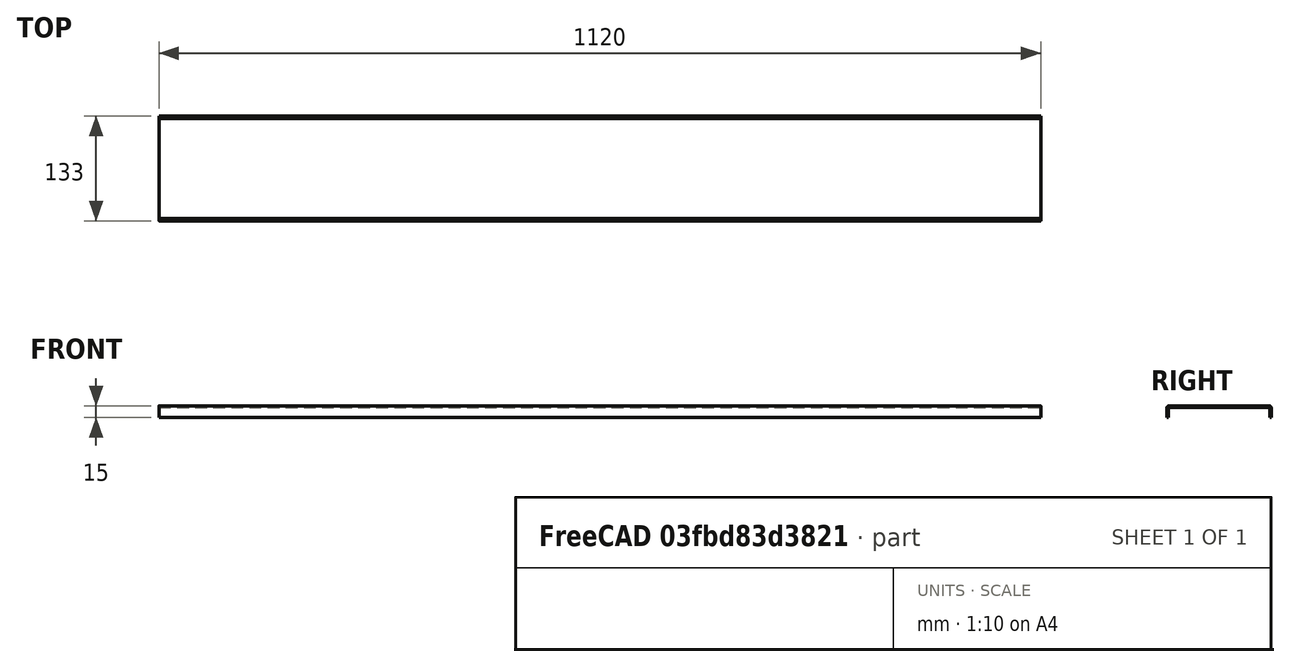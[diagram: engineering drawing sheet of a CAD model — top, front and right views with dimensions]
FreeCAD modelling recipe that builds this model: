
FCSTD DOCUMENT  (FreeCAD 0.17R13528 (Git))
Label: SupportClavierSuperieur
License: All rights reserved
LicenseURL: http://en.wikipedia.org/wiki/All_rights_reserved
objects: Drawing::FeatureViewPart×3, Drawing::FeatureViewPython×3, Part::FeaturePython×2, Part::Box×1, PartDesign::FeatureBase×1, PartDesign::Body×1, Drawing::FeaturePage×1
note: 5 computed .brp shape members not serialized (recipe doc carries the construction recipe); baked Part::Feature solids carry a one-line shape summary decoded from their .brp

FEATURE [Part::Box] Box  label="Cube"
  AttacherType = Attacher::AttachEngine3D
  Height = 2
  Length = 1120
  Width = 127
FEATURE [Part::FeaturePython] Bend  # WARN: FeaturePython — macro-defined, semantics opaque (R4)
  angle = 90
  baseObject = -> Box [Face3]
  gap1 = 0
  gap2 = 0
  invert = true
  length = 12
  radius = 1
  reliefd = 1
  reliefw = 0.5
FEATURE [Part::FeaturePython] Bend001  # WARN: FeaturePython — macro-defined, semantics opaque (R4)
  angle = 90
  baseObject = -> Bend [Face14]
  gap1 = 0
  gap2 = 0
  invert = true
  length = 12
  radius = 1
  reliefd = 1
  reliefw = 0.5
FEATURE [PartDesign::FeatureBase] BaseFeature
  BaseFeature = -> Bend001
FEATURE [PartDesign::Body] Body
  BaseFeature = -> Bend001
  Group = -> [BaseFeature]
  Origin = -> Origin
  Tip = -> BaseFeature
FEATURE [Drawing::FeatureViewPart] Ortho  label="Ortho_0_0"
  Direction = (0,0,1)
  HiddenWidth = 0.15
  LineWidth = 0.35
  Rotation = 0
  Scale = 0.2
  ShowHiddenLines = false
  ShowSmoothLines = false
  Source = -> Body
  Tolerance = 0.05
  ViewResult = <g id="Ortho_0_0"\n   transform="rotate(0,26.6667,120.6) translate(26.6667,120.6) scale(0.2,0.2)"\n  >\n<g   fill="none"\n   stroke="rgb(0, 0, 0)"\n   stroke-linecap="butt"\n   stroke-linejoin="miter"\n   stroke-width="1.750000"\n   transform="scale(1,-1)"\n  >\n<path id= "1" d=" M 0 130 L 1120 130 " />\n<path d="M1120,127 L1120,127.336  L1120,127.668  L1120,127.991  L1120,128.302  L1120,128.596  L1120,128.87  L1120,129.121  L1120,129.345  L1120,129.54  L1120,129.703  L1120,129.832  L1120,129.925  L1120,129.981  L1120,130 " /><path id= "3" d=" M 0 127 L 1120 127 " />\n<path d="M0,127 L0,127.336  L0,127.668  L0,127.991  L0,128.302  L0,128.596  L0,128.87  L0,129.121  L0,129.345  L0,129.54  L0,129.703  L0,129.832  L0,129.925  L0,129.981  L0,130 " /><path id= "5" d=" M 1120 0 L 1120 127 " />\n<path id= "6" d=" M 0 0 L 0 127 " />\n<path id= "7" d=" M 0 0 L 1120 0 " />\n<path d="M1120,0 L1120,-0.335893  L1120,-0.667563  L1120,-0.990837  L1120,-1.30165  L1120,-1.5961  L1120,-1.87047  L1120,-2.12132  L1120,-2.34549  L1120,-2.54017  L1120,-2.70291  L1120,-2.83165  L1120,-2.92478  L1120,-2.98114  L1120,-3 " /><path id= "9" d=" M 0 -3 L 1120 -3 " />\n<path d="M0,0 L0,-0.335893  L0,-0.667563  L0,-0.990837  L0,-1.30165  L0,-1.5961  L0,-1.87047  L0,-2.12132  L0,-2.34549  L0,-2.54017  L0,-2.70291  L0,-2.83165  L0,-2.92478  L0,-2.98114  L0,-3 " /></g>\n</g>
  Visible = false
  X = 26.6667
  Y = 120.6
FEATURE [Drawing::FeatureViewPart] Ortho001  label="Ortho_1_0"
  Direction = (-1,0,0)
  HiddenWidth = 0.15
  LineWidth = 0.35
  Rotation = 180
  Scale = 0.2
  ShowHiddenLines = false
  ShowSmoothLines = false
  Source = -> Body
  Tolerance = 0.05
  ViewResult = <g id="Ortho_1_0"\n   transform="rotate(180,269.933,120.6) translate(269.933,120.6) scale(0.2,0.2)"\n  >\n<g   fill="none"\n   stroke="rgb(0, 0, 0)"\n   stroke-linecap="butt"\n   stroke-linejoin="miter"\n   stroke-width="1.750000"\n   transform="scale(1,-1)"\n  >\n<path id= "1" d=" M 13 -128 L 13 -130 " />\n<path id= "2" d=" M 1 -128 L 13 -128 " />\n<path id= "3" d=" M 1 -130 L 13 -130 " />\n<path id= "4" d=" M 1 -128 L 1 -130 " />\n<path d="M0 -127 A1 1 0 0 1 1 -128" /><path d="M-2 -127 A3 3 0 0 1 1 -130" /><path id= "7" d=" M 0 -127 L -2 -127 " />\n<path id= "8" d=" M 0 0 L 0 -127 " />\n<path id= "9" d=" M -2 0 L -2 -127 " />\n<path id= "10" d=" M 0 0 L -2 0 " />\n<path d="M0 0 A1 1 0 0 0 1 1" /><path d="M-2 0 A3 3 0 0 0 1 3" /><path id= "13" d=" M 1 1 L 1 3 " />\n<path id= "14" d=" M 1 1 L 13 1 " />\n<path id= "15" d=" M 1 3 L 13 3 " />\n<path id= "16" d=" M 13 1 L 13 3 " />\n</g>\n</g>
  Visible = false
  X = 269.933
  Y = 120.6
FEATURE [Drawing::FeatureViewPart] Ortho002  label="Ortho_0_1"
  Direction = (0,-1,0)
  HiddenWidth = 0.15
  LineWidth = 0.35
  Rotation = 90
  Scale = 0.2
  ShowHiddenLines = false
  ShowSmoothLines = false
  Source = -> Body
  Tolerance = 0.05
  ViewResult = <g id="Ortho_0_1"\n   transform="rotate(90,26.6667,51.2) translate(26.6667,51.2) scale(0.2,0.2)"\n  >\n<g   fill="none"\n   stroke="rgb(0, 0, 0)"\n   stroke-linecap="butt"\n   stroke-linejoin="miter"\n   stroke-width="1.750000"\n   transform="scale(1,-1)"\n  >\n<path id= "1" d=" M -2 0 L -2 1120 " />\n<path d="M-2,1120 Q-1.99057,1120 -1.98114,1120  Q-1.95296,1120 -1.92478,1120  Q-1.87822,1120 -1.83165,1120  Q-1.76728,1120 -1.70291,1120  Q-1.62154,1120 -1.54017,1120  Q-1.44283,1120 -1.34549,1120  Q-1.23341,1120 -1.12132,1120  Q-0.995895,1120 -0.870469,1120  Q-0.733283,1120 -0.596096,1120  Q-0.448874,1120 -0.301651,1120  Q-0.146244,1120 0.00916281,1120  Q0.1708,1120 0.332437,1120  Q0.662922,1120 1,1120 " /><path id= "3" d=" M 1 0 L 1 1120 " />\n<path d="M-2,0 Q-1.99057,0 -1.98114,0  Q-1.95296,0 -1.92478,0  Q-1.87822,0 -1.83165,0  Q-1.76728,0 -1.70291,0  Q-1.62154,0 -1.54017,0  Q-1.44283,0 -1.34549,0  Q-1.23341,0 -1.12132,0  Q-0.995895,0 -0.870469,0  Q-0.733283,0 -0.596096,0  Q-0.448874,0 -0.301651,0  Q-0.146244,0 0.00916281,0  Q0.1708,0 0.332437,0  Q0.662922,0 1,0 " /><path id= "5" d=" M 1 1120 L 13 1120 " />\n<path id= "6" d=" M 13 0 L 13 1120 " />\n<path id= "7" d=" M 1 0 L 13 0 " />\n</g>\n</g>
  Visible = false
  X = 26.6667
  Y = 51.2
FEATURE [Drawing::FeatureViewPython] dim001  # drawing view (typed FeaturePython)
  Rotation = 0
  ViewResult = <g> \n  <line x1="26.666700" y1="55.800000" x2="26.666700" y2="66.000000" style="stroke:rgb(0,0,255);stroke-width:0.30" />\n<line x1="250.666700" y1="55.800000" x2="250.666700" y2="66.000000" style="stroke:rgb(0,0,255);stroke-width:0.30" />\n<line x1="26.666700" y1="65.000000" x2="250.666700" y2="65.000000" style="stroke:rgb(0,0,255);stroke-width:0.30" /> \n  <polygon points="250.666700,65.000000 247.666700,64.000000 246.666700,65.000000 247.666700,66.000000" style="fill:rgb(0,0,255);stroke:rgb(0,0,255);stroke-width:0" /><polygon points="26.666700,65.000000 29.666700,66.000000 30.666700,65.000000 29.666700,64.000000" style="fill:rgb(0,0,255);stroke:rgb(0,0,255);stroke-width:0" /> \n  <text x="138.666700" y="63.000000" font-family="Verdana" font-size="3.6" fill="rgb(0,0,255)" text-anchor="middle" transform="rotate(0.000000 138.666700,63.000000)" >1120</text> </g>
  Visible = false
  X = 0
  Y = 0
  arrowL1 = 3
  arrowL2 = 1
  arrowW = 2
  arrow_scheme = 0
  autoPlaceOffset = 2
  autoPlaceText = true
  click1_x = 125
  click1_y = 65
  click2_x = 125
  click2_y = 65
  comma_decimal_place = false
  dimension_line_overshoot = 1
  gap_datum_points = 2
  halfDimension_linear = false
  lineColor = rgb(0,0,255)
  strokeWidth = 0.3
  textFormat_linear = %(value)3.0f
  textRenderer_color = rgb(0,0,255)
  textRenderer_family = Verdana
  textRenderer_size = 3.6
  unit_custom_scale = 1
  unit_scheme = 0
FEATURE [Drawing::FeatureViewPython] dim002  # drawing view (typed FeaturePython)
  Rotation = 0
  ViewResult = <g> <line x1="24.666700" y1="94.600000" x2="19.000000" y2="94.600000" style="stroke:rgb(0,0,255);stroke-width:0.30" />\n<line x1="24.666700" y1="121.200000" x2="19.000000" y2="121.200000" style="stroke:rgb(0,0,255);stroke-width:0.30" />\n<line x1="20.000000" y1="94.600000" x2="20.000000" y2="121.200000" style="stroke:rgb(0,0,255);stroke-width:0.30" />\n<polygon points="20.000000,94.600000 19.000000,97.600000 20.000000,98.600000 21.000000,97.600000" style="fill:rgb(0,0,255);stroke:rgb(0,0,255);stroke-width:0" />\n<polygon points="20.000000,121.200000 21.000000,118.200000 20.000000,117.200000 19.000000,118.200000" style="fill:rgb(0,0,255);stroke:rgb(0,0,255);stroke-width:0" />\n<text x="18.000000" y="107.900000" font-family="Verdana" font-size="3.6" fill="rgb(0,0,255)" text-anchor="middle" transform="rotate(-90.000000 18.000000,107.900000)" >133</text> </g> 
  Visible = false
  X = 0
  Y = 0
  arrowL1 = 3
  arrowL2 = 1
  arrowW = 2
  arrow_scheme = 0
  autoPlaceOffset = 2
  autoPlaceText = true
  click1_x = 20
  click1_y = 120
  click2_x = 20
  click2_y = 120
  comma_decimal_place = false
  dimension_line_overshoot = 1
  gap_datum_points = 2
  halfDimension_linear = false
  lineColor = rgb(0,0,255)
  strokeWidth = 0.3
  textFormat_linear = %(value)3.0f
  textRenderer_color = rgb(0,0,255)
  textRenderer_family = Verdana
  textRenderer_size = 3.6
  unit_custom_scale = 1
  unit_scheme = 0
FEATURE [Drawing::FeatureViewPython] dim003  # drawing view (typed FeaturePython)
  Rotation = 0
  ViewResult = <g> <line x1="270.333000" y1="122.600000" x2="270.333000" y2="131.000000" style="stroke:rgb(0,0,255);stroke-width:0.30" />\n<line x1="267.333000" y1="123.200025" x2="267.333000" y2="131.000000" style="stroke:rgb(0,0,255);stroke-width:0.30" />\n<line x1="270.333000" y1="130.000000" x2="267.333000" y2="130.000000" style="stroke:rgb(0,0,255);stroke-width:0.30" />\n<polygon points="270.333000,130.000000 273.333000,131.000000 274.333000,130.000000 273.333000,129.000000" style="fill:rgb(0,0,255);stroke:rgb(0,0,255);stroke-width:0" />\n<polygon points="267.333000,130.000000 264.333000,129.000000 263.333000,130.000000 264.333000,131.000000" style="fill:rgb(0,0,255);stroke:rgb(0,0,255);stroke-width:0" />\n<text x="268.833000" y="128.000000" font-family="Verdana" font-size="3.6" fill="rgb(0,0,255)" text-anchor="middle" transform="rotate(0.000000 268.833000,128.000000)" > 15</text> </g> 
  Visible = false
  X = 0
  Y = 0
  arrowL1 = 3
  arrowL2 = 1
  arrowW = 2
  arrow_scheme = 0
  autoPlaceOffset = 2
  autoPlaceText = true
  click1_x = 265
  click1_y = 130
  click2_x = 265
  click2_y = 130
  comma_decimal_place = false
  dimension_line_overshoot = 1
  gap_datum_points = 2
  halfDimension_linear = false
  lineColor = rgb(0,0,255)
  strokeWidth = 0.3
  textFormat_linear = %(value)3.0f
  textRenderer_color = rgb(0,0,255)
  textRenderer_family = Verdana
  textRenderer_size = 3.6
  unit_custom_scale = 1
  unit_scheme = 0
FEATURE [Drawing::FeaturePage] Page
  EditableTexts = G.Bachelier | Support clavier | Vue générale | Acier épaisseur 2mm | A4 | X / Y | 1/5 | 2 | 1 | 14/08/2018 | REV B
  Group = -> [Ortho,Ortho001,Ortho002,dim001,dim002,dim003]
  Template = <path>
note: 1 file-system path scrubbed to <path> (originals preserved in the JSON sidecar)
